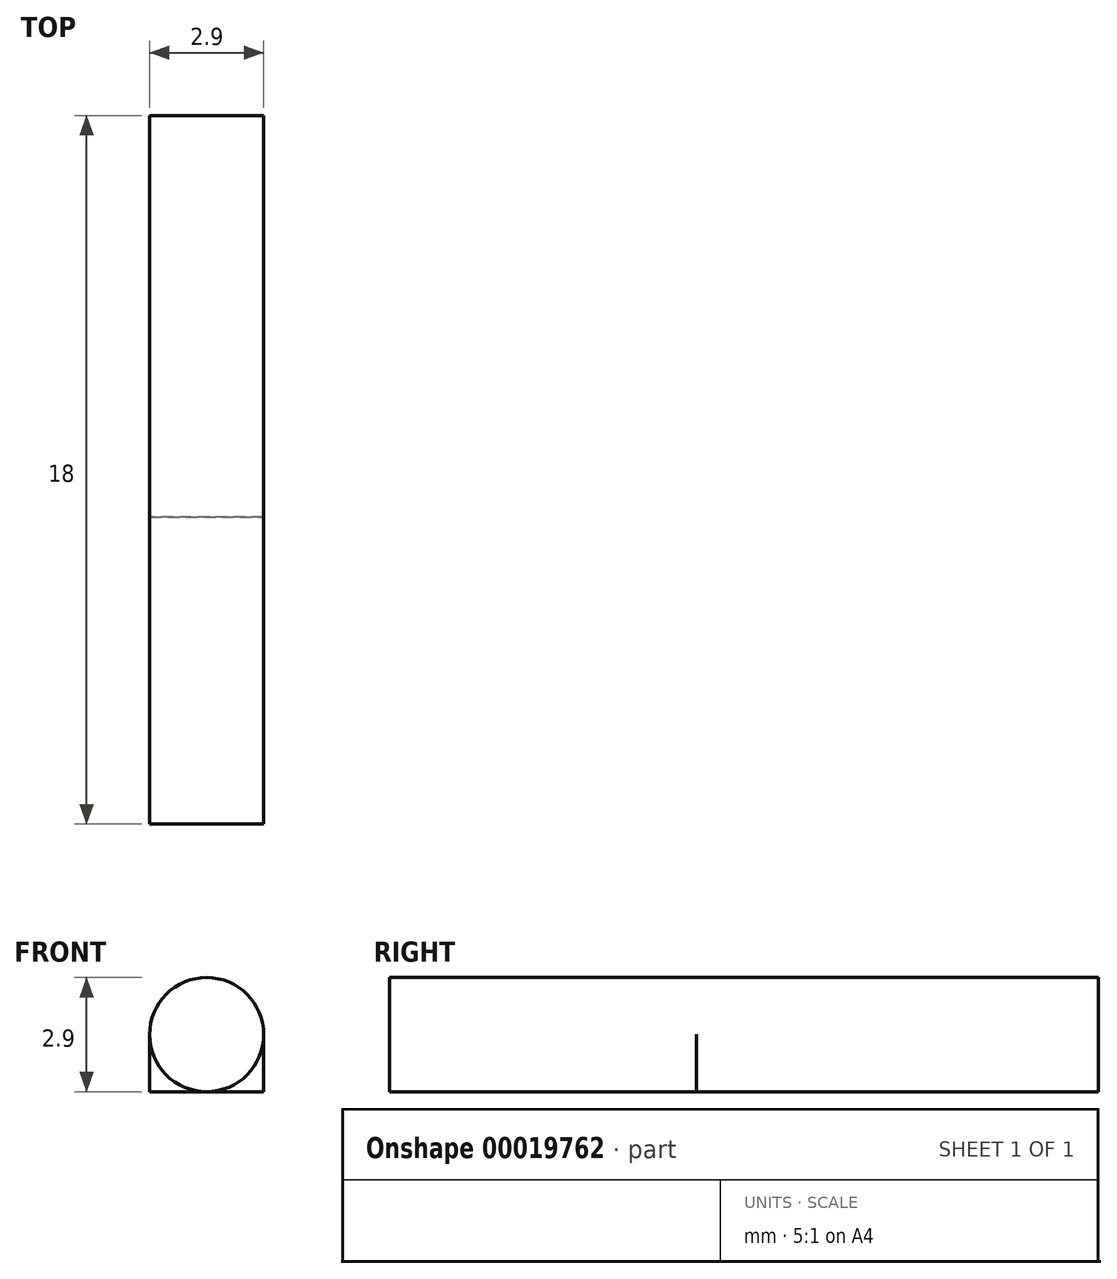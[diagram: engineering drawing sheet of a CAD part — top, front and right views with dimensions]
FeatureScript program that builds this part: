
annotation { "Feature Type Name" : "Feature", "Feature Type Description" : "" }
export const myFeature = defineFeature(function(context is Context, id is Id, definition is map)
    precondition{}
    {
        {
            var Q0;
            Q0=qCreatedBy(makeId("Front.planeOp"),FACE);
            var sketch = newSketch(context, id + "F0", { "sketchPlane" : qUnion([Q0])});
            skCircle(sketch, "E0", {"center": v(0, 0) * mm, "radius": 1.45 * mm});
            skPoint(sketch, "E1.rect.middle", {"position": v(0, -1.45) * mm});
            skLineSegment(sketch, "E2.rect.top", {"start": v(1.45, -1.45) * mm, "end": v(-1.45, -1.45) * mm});
            skLineSegment(sketch, "E3", {"start": v(-1.45, 0) * mm, "end": v(-1.45, -1.45) * mm});
            skLineSegment(sketch, "E4", {"start": v(1.45, 0) * mm, "end": v(1.45, -1.45) * mm});
            skSolve(sketch);
        }
        {
            var Q0;
            {var subQ0=sQuery(id+"F0.wireOp",EDGE,"E0");var subQ2=makeQuery(id+"F0.imprint","INTERSECT",VERTEX,{"derivedFrom":[subQ0,sQuery(id+"F0.wireOp",EDGE,"E3")]});Q0=makeQuery(id+"F0.imprint","IMPRINT",FACE,{"disambiguationData":[TD([[makeQuery(id+"F0.imprint","IMPRINT",EDGE,{"disambiguationData":[TD([[subQ2,1.0]])],"derivedFrom":subQ0}),1.0]])]});}
            extrude(context, id + "F1", {"entities" : qUnion([Q0]), "depth" : 18 * mm});
        }
        {
            var Q0;
            Q0=makeQuery(id+"F0.imprint","IMPRINT",FACE,{"disambiguationData":[TD([[makeQuery(id+"F0.imprint","IMPRINT",EDGE,{"derivedFrom":sQuery(id+"F0.wireOp",EDGE,"E2.rect.top")}),-1.0]])]});
            extrude(context, id + "F2", {"entities" : qUnion([Q0]), "operationType" : NewBodyOperationType.ADD, "depth" : 10.2 * mm});
        }
    });
